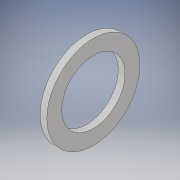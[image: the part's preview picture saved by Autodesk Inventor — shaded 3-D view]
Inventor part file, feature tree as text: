
AUTODESK INVENTOR PART (.ipt)
format: ipt  version: 2019 (Build 230136000, 136)  size: 219,136 bytes
history: native  units: in
note: dims shown in document units (in); Inventor stores cm internally (conversion verified against a paired STEP export)
features: fillet x14, sketch x9, extrude x7, mirror x2, projected_geometry x2, plane x1, pattern_circular x1
ambient origin geometry x8: Origin, YZ Plane, XZ Plane, XY Plane, X Axis, Y Axis, Z Axis, Center Point
bodies: Solid1 (feature_tree)
feature tree (36):
  extrude  "Extrusion1"  Depth=0.4331in
  extrude  "Extrusion2"  Depth=0.1969in
  mirror  "Mirror1"
  extrude  "Extrusion3"  Depth=0.3603in
  plane  "Work Plane1"
  extrude  "Extrusion4"  Depth=0.1181in
  extrude  "Extrusion5"  Depth=1.1811in TaperAngle=0.0deg
  pattern_circular  "Circular Pattern1"  Count=3  [1 undecoded]
  extrude  "Extrusion6"  Depth=0.1969in TaperAngle=0.0deg
  extrude  "Extrusion7"  Depth=0.1969in
  mirror  "Mirror2"
  sketch  "Sketch12"  dims[d53=0.122in]
  sketch  "Sketch14"  dims[d55=0.0787in d56=0.0787in d57=0.0591in d58=0.0787in d59=0.0787in d60=0.0787in d61=0.0787in d62=0.0787in d63=0.0787in d64=0.1969in d65=0.0591in d66=0.0591in d67=0.0591in d68=0.0591in d69=0.0591in]
  fillet  "Fillet2"  Radius=0.7874in
  fillet  "Fillet3"  Radius=1.1811in
  fillet  "Fillet4"  Radius=2.1654in
  fillet  "Fillet5"  Radius=0.2756in
  fillet  "Fillet6"  Radius=0.1969in
  fillet  "Fillet7"  Radius=0.1969in
  fillet  "Fillet8"  Radius=0.2756in
  fillet  "Fillet9"  Radius=0.2756in
  fillet  "Fillet10"  Radius=1.1811in
  fillet  "Fillet11"  Radius=0.122in
  fillet  "Fillet12"  Radius=0.1969in
  fillet  "Fillet13"  Radius=0.4724in
  fillet  "Fillet14"  Radius=0.0787in
  fillet  "Fillet15"  [1 undecoded]
  sketch  "Sketch2"  dims[d4=2.7165in d5=0.4331in]
  sketch  "Sketch4"  dims[d6=0.1969in d7=0.0in d16=0.5118in]
  sketch  "Sketch5"  dims[d17=0.5118in d18=0.3603in]
  projected_geometry  "Projected Loop1"
  sketch  "Sketch6"  dims[d20=0.1181in d21=0.1181in]
  projected_geometry  "Projected Loop2"
  sketch  "Sketch9"  dims[d22=180.0deg d23=1.1811in d24=0.0in d25=1.1811in d26=0.0in]
  sketch  "Sketch10"  dims[d27=-1.1811in d28=0.1969in d29=0.0in]
  sketch  "Sketch11"  dims[d32=2.1654in d33=0.2441in d34=0.7874in d35=0.0in d36=1.1811in d37=360.0deg d39=2.1654in d40=0.2756in d41=0.1969in d42=0.1969in d43=0.2756in d44=0.2756in d45=1.1811in d46=0.0in d47=0.122in d48=0.1969in d49=0.0in d50=0.4724in d51=0.0787in d52=90.0deg]
note: 2 required parameter values undecoded (feature->parameter linkage not recoverable at this tier; creation-order binding heuristic only, values carry confidence <= 0.55)
